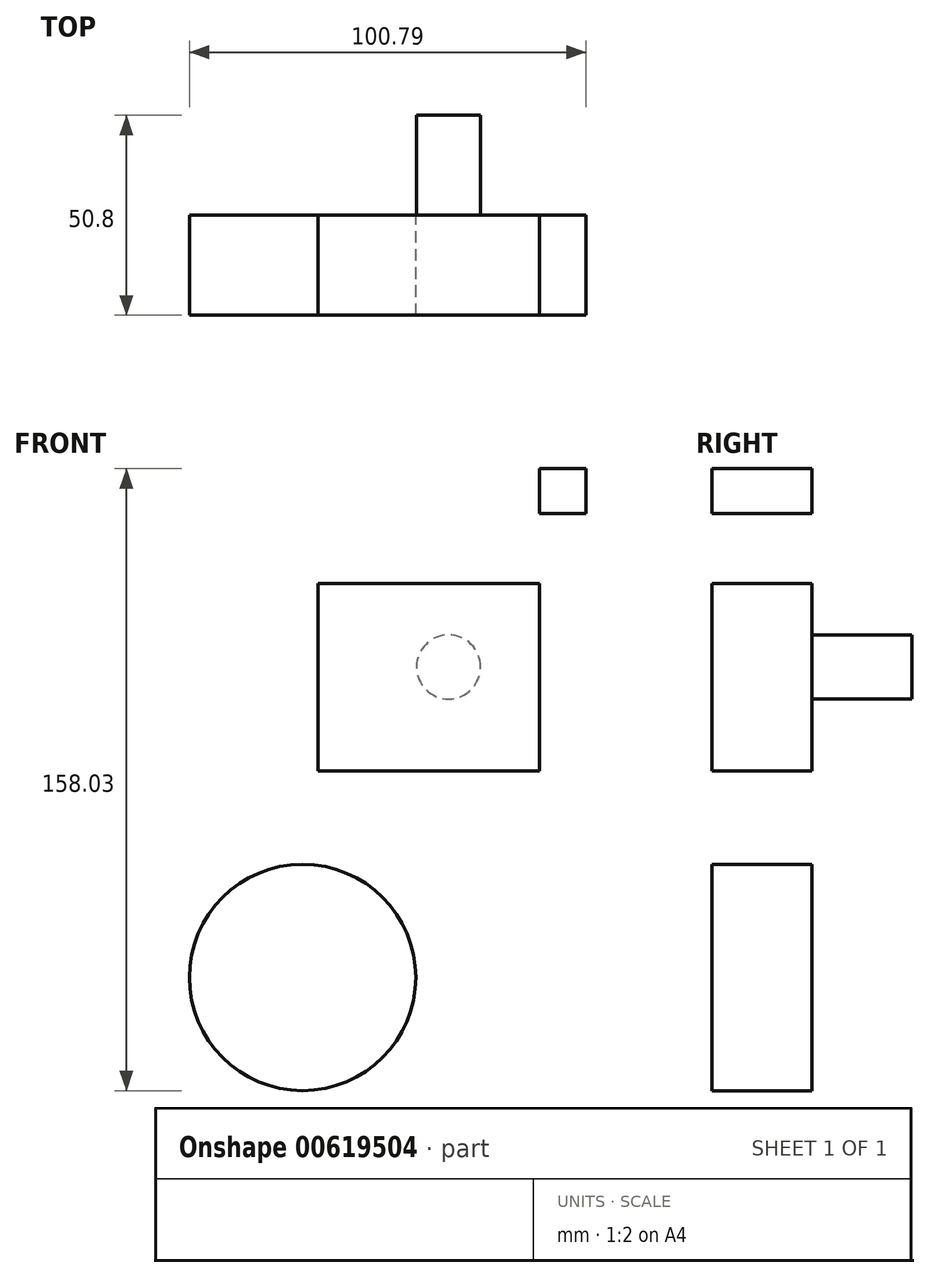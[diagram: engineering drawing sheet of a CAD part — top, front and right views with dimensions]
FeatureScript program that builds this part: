
annotation { "Feature Type Name" : "Feature", "Feature Type Description" : "" }
export const myFeature = defineFeature(function(context is Context, id is Id, definition is map)
    precondition{}
    {
        {
            var Q0;
            Q0=qCreatedBy(makeId("Front.planeOp"),FACE);
            var sketch = newSketch(context, id + "F0", { "sketchPlane" : qUnion([Q0])});
            skLineSegment(sketch, "E0.bottom", {"start": v(72.03, 77.1) * mm, "end": v(60.13, 77.1) * mm});
            skLineSegment(sketch, "E0.top", {"start": v(72.03, 65.72) * mm, "end": v(60.13, 65.72) * mm});
            skLineSegment(sketch, "E0.left", {"start": v(72.03, 77.1) * mm, "end": v(72.03, 65.72) * mm});
            skLineSegment(sketch, "E0.right", {"start": v(60.13, 77.1) * mm, "end": v(60.13, 65.72) * mm});
            skLineSegment(sketch, "E1.bottom", {"start": v(3.87, 0.27) * mm, "end": v(60.13, 0.27) * mm});
            skLineSegment(sketch, "E1.top", {"start": v(3.87, 47.9) * mm, "end": v(60.13, 47.9) * mm});
            skLineSegment(sketch, "E1.left", {"start": v(3.87, 0.27) * mm, "end": v(3.87, 47.9) * mm});
            skLineSegment(sketch, "E1.right", {"start": v(60.13, 0.27) * mm, "end": v(60.13, 47.9) * mm});
            skSolve(sketch);
        }
        {
            var Q0;
            Q0 = qSketchRegion(id + "F0", true);
            extrude(context, id + "F1", {"entities" : qUnion([Q0]), "depth" : 25.4 * mm, "offsetDistance" : 25.4 * mm});
        }
        {
            var Q0;
            Q0=makeQuery(id+"F1.opExtrude","CAP_FACE",FACE,{"disambiguationData":[OSD([sQuery(id+"F0.wireOp",EDGE,"E1.bottom"),sQuery(id+"F0.wireOp",EDGE,"E1.top"),sQuery(id+"F0.wireOp",EDGE,"E1.left"),sQuery(id+"F0.wireOp",EDGE,"E1.right")])],"isStart":true});
            var sketch = newSketch(context, id + "F2", { "sketchPlane" : qUnion([Q0])});
            skCircle(sketch, "E2", {"center": v(-37.08, 26.73) * mm, "radius": 8.15 * mm});
            skSolve(sketch);
        }
        {
            var Q0;
            Q0 = qSketchRegion(id + "F2", true);
            extrude(context, id + "F3", {"entities" : qUnion([Q0]), "operationType" : NewBodyOperationType.ADD, "depth" : 25.4 * mm, "offsetDistance" : 25.4 * mm});
        }
        {
            var Q0;
            Q0=makeQuery(id+"F1.opExtrude","SWEPT_FACE",FACE,{"disambiguationData":[OSD([sQuery(id+"F0.wireOp",EDGE,"E1.top")])]});
            var sketch = newSketch(context, id + "F4", { "sketchPlane" : qUnion([Q0])});
            skSolve(sketch);
        }
        {
            var Q0;
            Q0=qCreatedBy(makeId("Front.planeOp"),FACE);
            var sketch = newSketch(context, id + "F5", { "sketchPlane" : qUnion([Q0])});
            skCircle(sketch, "E3", {"center": v(0, -52.18) * mm, "radius": 28.76 * mm});
            skSolve(sketch);
        }
        {
            var Q0;
            Q0 = qSketchRegion(id + "F5", true);
            extrude(context, id + "F6", {"entities" : qUnion([Q0]), "depth" : 25.4 * mm, "offsetDistance" : 25.4 * mm});
        }
    });
